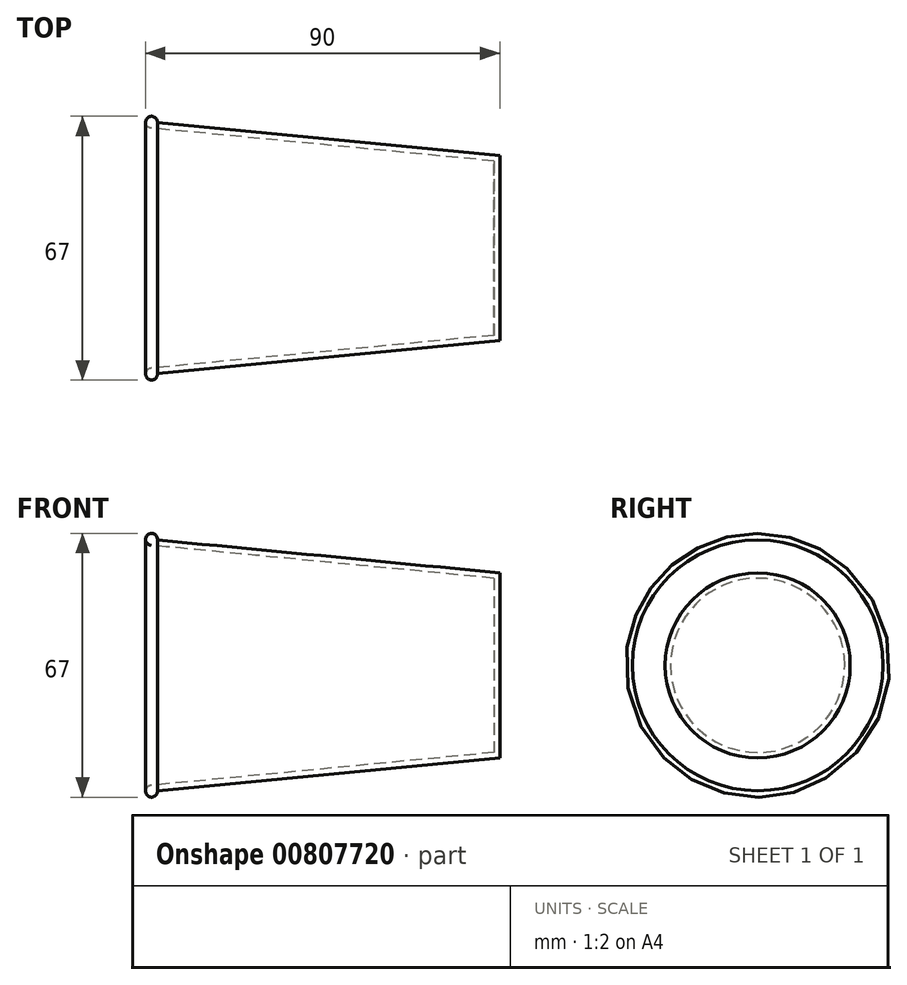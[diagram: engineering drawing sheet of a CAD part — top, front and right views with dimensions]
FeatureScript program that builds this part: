
annotation { "Feature Type Name" : "Feature", "Feature Type Description" : "" }
export const myFeature = defineFeature(function(context is Context, id is Id, definition is map)
    precondition{}
    {
        {
            var Q0;
            Q0=qCreatedBy(makeId("Top.planeOp"),FACE);
            var sketch = newSketch(context, id + "F0", { "sketchPlane" : qUnion([Q0])});
            skLineSegment(sketch, "E0", {"start": v(50.01, 23.5) * mm, "end": v(50.01, 0) * mm});
            skLineSegment(sketch, "E1", {"start": v(50.01, 0) * mm, "end": v(-53.95, 0) * mm});
            skLineSegment(sketch, "E2", {"start": v(-132.47, 0) * mm, "end": v(167.98, 0) * mm, "construction": true});
            skLineSegment(sketch, "E3", {"start": v(-38.63, 30.5) * mm, "end": v(48.51, 22.14) * mm});
            skLineSegment(sketch, "E4", {"start": v(48.51, 22.14) * mm, "end": v(48.51, 0) * mm});
            skArc(sketch, "E5", {"start": v(-37, 31.86) * mm, "mid": v(-39.44, 33.16) * mm, "end": v(-38.63, 30.5) * mm});
            skLineSegment(sketch, "E6.trimOffspring", {"start": v(-37, 31.86) * mm, "end": v(50.01, 23.5) * mm});
            skSolve(sketch);
        }
        {
            var Q0;
            Q0 = qSketchRegion(id + "F0", true);
            var Q1;
            Q1=sQuery(id+"F0.wireOp",EDGE,"E2");
            revolve(context, id + "F1", {"surfaceOperationType" : NewSurfaceOperationType.NEW, "entities" : qUnion([Q0]), "axis" : qUnion([Q1]), "revolveType" : RevolveType.FULL});
        }
    });
